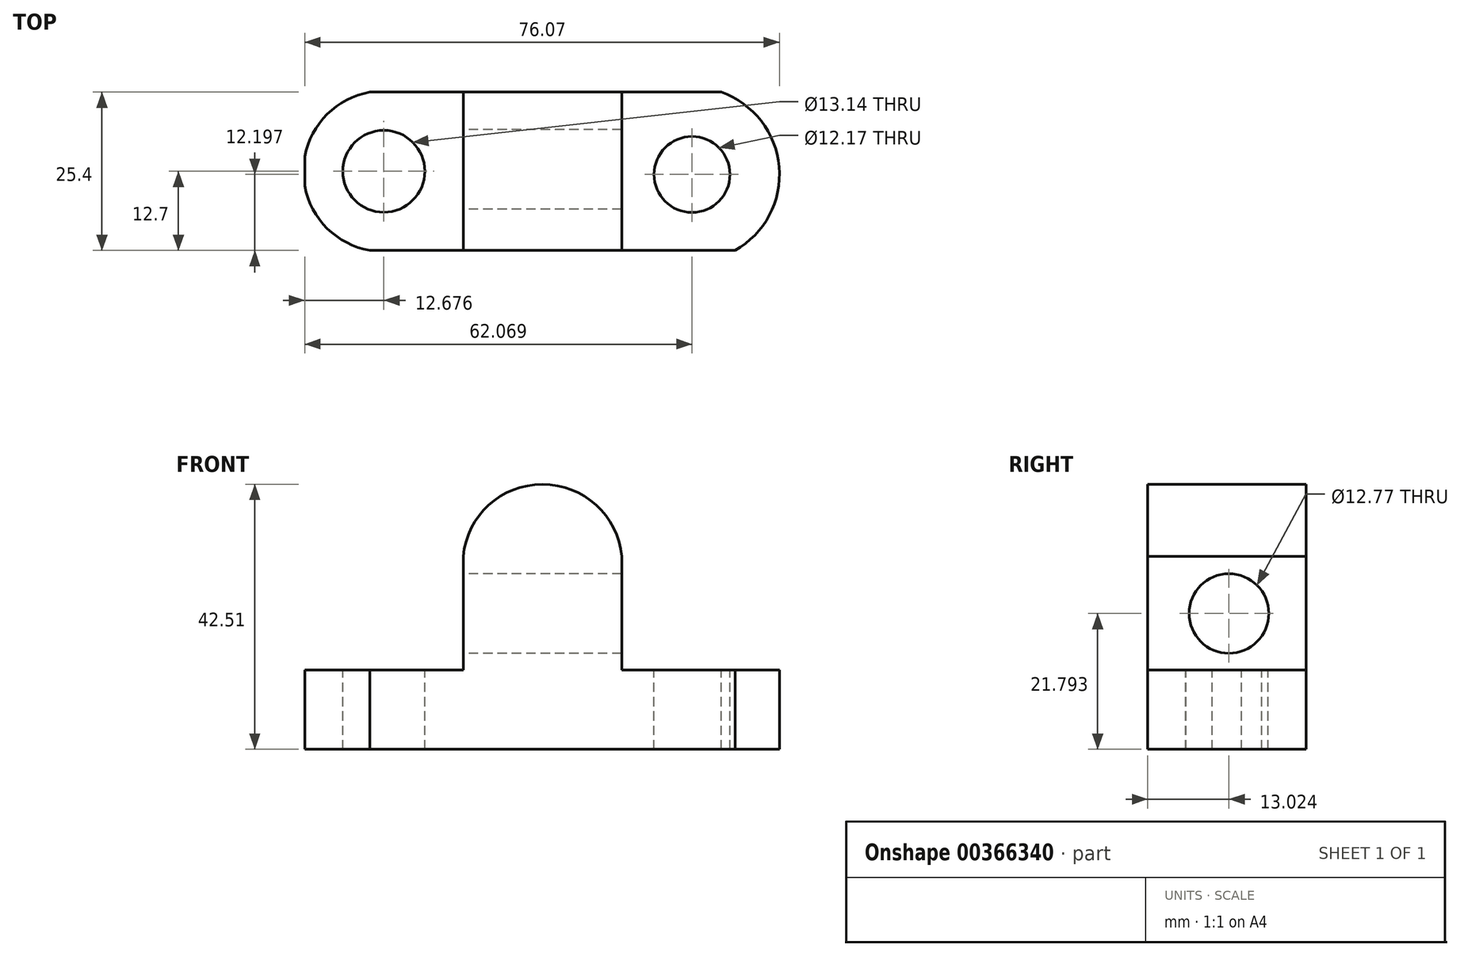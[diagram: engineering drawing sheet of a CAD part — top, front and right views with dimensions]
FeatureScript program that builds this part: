
annotation { "Feature Type Name" : "Feature", "Feature Type Description" : "" }
export const myFeature = defineFeature(function(context is Context, id is Id, definition is map)
    precondition{}
    {
        {
            var Q0;
            Q0=qCreatedBy(makeId("Front.planeOp"),FACE);
            var sketch = newSketch(context, id + "F0", { "sketchPlane" : qUnion([Q0])});
            skLineSegment(sketch, "E0", {"start": v(0, 0) * mm, "end": v(0, 12.7) * mm});
            skLineSegment(sketch, "E1", {"start": v(0, 12.7) * mm, "end": v(25.4, 12.7) * mm});
            skLineSegment(sketch, "E2", {"start": v(25.4, 12.7) * mm, "end": v(25.4, 44.45) * mm});
            skLineSegment(sketch, "E3", {"start": v(25.4, 44.45) * mm, "end": v(50.8, 44.45) * mm});
            skLineSegment(sketch, "E4", {"start": v(50.8, 44.45) * mm, "end": v(50.8, 12.7) * mm});
            skLineSegment(sketch, "E5", {"start": v(50.8, 12.7) * mm, "end": v(76.2, 12.7) * mm});
            skLineSegment(sketch, "E6", {"start": v(76.2, 12.7) * mm, "end": v(76.2, 0) * mm});
            skLineSegment(sketch, "E7", {"start": v(76.2, 0) * mm, "end": v(0, 0) * mm});
            skSolve(sketch);
        }
        {
            var Q0;
            Q0 = qSketchRegion(id + "F0", true);
            extrude(context, id + "F1", {"entities" : qUnion([Q0]), "depth" : 25.4 * mm});
        }
        {
            var Q0;
            Q0=makeQuery(id+"F1.opExtrude","CAP_FACE",FACE,{"disambiguationData":[OSD([sQuery(id+"F0.wireOp",EDGE,"E0"),sQuery(id+"F0.wireOp",EDGE,"E1"),sQuery(id+"F0.wireOp",EDGE,"E2"),sQuery(id+"F0.wireOp",EDGE,"E3"),sQuery(id+"F0.wireOp",EDGE,"E4"),sQuery(id+"F0.wireOp",EDGE,"E5"),sQuery(id+"F0.wireOp",EDGE,"E6"),sQuery(id+"F0.wireOp",EDGE,"E7")])],"isStart":false});
            var sketch = newSketch(context, id + "F2", { "sketchPlane" : qUnion([Q0])});
            skArc(sketch, "E8", {"start": v(50.8, 28.58) * mm, "mid": v(38.1, 42.5) * mm, "end": v(25.4, 28.58) * mm});
            skSolve(sketch);
        }
        {
            var Q0;
            Q0 = qSketchRegion(id + "F2", true);
            var Q1;
            {var subQ5=makeQuery(id+"F1.opExtrude","CAP_EDGE",EDGE,{"disambiguationData":[OSD([sQuery(id+"F0.wireOp",EDGE,"E3")])],"isStart":false});Q1=makeQuery(id+"F2.imprint","IMPRINT",FACE,{"disambiguationData":[TD([[makeQuery(id+"F2.imprint","IMPRINT",EDGE,{"derivedFrom":subQ5}),-1.0]])]});}
            extrude(context, id + "F3", {"entities" : qUnion([Q0, Q1]), "operationType" : NewBodyOperationType.REMOVE, "oppositeDirection" : true, "depth" : 25.4 * mm});
        }
        {
            var Q0;
            Q0=makeQuery(id+"F1.opExtrude","SWEPT_FACE",FACE,{"disambiguationData":[OSD([sQuery(id+"F0.wireOp",EDGE,"E1")])]});
            var sketch = newSketch(context, id + "F4", { "sketchPlane" : qUnion([Q0])});
            skArc(sketch, "E9", {"start": v(10.45, 0) * mm, "mid": v(-0.22, -12.7) * mm, "end": v(10.45, -25.4) * mm});
            skArc(sketch, "E10", {"start": v(65.94, -25.4) * mm, "mid": v(76.07, -12.37) * mm, "end": v(65.13, 0) * mm});
            skSolve(sketch);
        }
        {
            var Q0;
            {var subQ0=sQuery(id+"F4.wireOp",EDGE,"E9");var subQ1=sQuery(id+"F0.wireOp",EDGE,"E1");var subQ2=makeQuery(id+"F1.opExtrude","CAP_EDGE",EDGE,{"disambiguationData":[OSD([subQ1])],"isStart":true});var subQ3=makeQuery(id+"F4.imprint","INTERSECT",VERTEX,{"derivedFrom":[subQ2,subQ0]});Q0=makeQuery(id+"F4.imprint","IMPRINT",FACE,{"disambiguationData":[TD([[makeQuery(id+"F4.imprint","IMPRINT",EDGE,{"disambiguationData":[TD([[subQ3,-1.0]])],"derivedFrom":subQ0}),-1.0]])]});}
            var Q1;
            {var subQ0=sQuery(id+"F4.wireOp",EDGE,"E9");var subQ1=sQuery(id+"F0.wireOp",EDGE,"E1");var subQ2=makeQuery(id+"F1.opExtrude","CAP_EDGE",EDGE,{"disambiguationData":[OSD([subQ1])],"isStart":false});var subQ3=makeQuery(id+"F4.imprint","INTERSECT",VERTEX,{"derivedFrom":[subQ2,subQ0]});Q1=makeQuery(id+"F4.imprint","IMPRINT",FACE,{"disambiguationData":[TD([[makeQuery(id+"F4.imprint","IMPRINT",EDGE,{"disambiguationData":[TD([[subQ3,1.0]])],"derivedFrom":subQ0}),-1.0]])]});}
            extrude(context, id + "F5", {"entities" : qUnion([Q0, Q1]), "operationType" : NewBodyOperationType.REMOVE, "oppositeDirection" : true, "depth" : 25.4 * mm});
        }
        {
            var Q0;
            Q0=makeQuery(id+"F1.opExtrude","SWEPT_FACE",FACE,{"disambiguationData":[OSD([sQuery(id+"F0.wireOp",EDGE,"E5")])]});
            var sketch = newSketch(context, id + "F6", { "sketchPlane" : qUnion([Q0])});
            skArc(sketch, "E11", {"start": v(68.95, -25.4) * mm, "mid": v(76.02, -11.99) * mm, "end": v(66.74, 0) * mm});
            skSolve(sketch);
        }
        {
            var Q0;
            Q0 = qSketchRegion(id + "F6", true);
            var Q1;
            {var subQ0=sQuery(id+"F6.wireOp",EDGE,"E11");Q1=makeQuery(id+"F6.imprint","IMPRINT",FACE,{"disambiguationData":[TD([[makeQuery(id+"F6.imprint","IMPRINT",EDGE,{"derivedFrom":subQ0}),-1.0]])]});}
            extrude(context, id + "F7", {"entities" : qUnion([Q0, Q1]), "operationType" : NewBodyOperationType.REMOVE, "oppositeDirection" : true, "depth" : 25.4 * mm});
        }
        {
            var Q0;
            Q0=makeQuery(id+"F1.opExtrude","SWEPT_FACE",FACE,{"disambiguationData":[OSD([sQuery(id+"F0.wireOp",EDGE,"E1")])]});
            var sketch = newSketch(context, id + "F8", { "sketchPlane" : qUnion([Q0])});
            skCircle(sketch, "E12", {"center": v(12.68, -12.7) * mm, "radius": 6.57 * mm});
            skSolve(sketch);
        }
        {
            var Q0;
            Q0=makeQuery(id+"F8.imprint","IMPRINT",FACE,{"disambiguationData":[TD([[makeQuery(id+"F8.imprint","IMPRINT",EDGE,{"derivedFrom":sQuery(id+"F8.wireOp",EDGE,"E12")}),1.0]])]});
            extrude(context, id + "F9", {"entities" : qUnion([Q0]), "operationType" : NewBodyOperationType.REMOVE, "oppositeDirection" : true, "depth" : 25.4 * mm});
        }
        {
            var Q0;
            Q0=makeQuery(id+"F1.opExtrude","SWEPT_FACE",FACE,{"disambiguationData":[OSD([sQuery(id+"F0.wireOp",EDGE,"E5")])]});
            var sketch = newSketch(context, id + "F10", { "sketchPlane" : qUnion([Q0])});
            skCircle(sketch, "E13", {"center": v(62.07, -13.2) * mm, "radius": 6.09 * mm});
            skSolve(sketch);
        }
        {
            var Q0;
            Q0=makeQuery(id+"F10.imprint","IMPRINT",FACE,{"disambiguationData":[TD([[makeQuery(id+"F10.imprint","IMPRINT",EDGE,{"derivedFrom":sQuery(id+"F10.wireOp",EDGE,"E13")}),1.0]])]});
            extrude(context, id + "F11", {"entities" : qUnion([Q0]), "operationType" : NewBodyOperationType.REMOVE, "oppositeDirection" : true, "depth" : 25.4 * mm});
        }
        {
            var Q0;
            Q0=makeQuery(id+"F1.opExtrude","SWEPT_FACE",FACE,{"disambiguationData":[OSD([sQuery(id+"F0.wireOp",EDGE,"E2")])]});
            var sketch = newSketch(context, id + "F12", { "sketchPlane" : qUnion([Q0])});
            skCircle(sketch, "E14", {"center": v(12.38, 21.8) * mm, "radius": 6.38 * mm});
            skSolve(sketch);
        }
        {
            var Q0;
            Q0 = qSketchRegion(id + "F12", true);
            extrude(context, id + "F13", {"entities" : qUnion([Q0]), "operationType" : NewBodyOperationType.REMOVE, "oppositeDirection" : true, "depth" : 25.4 * mm});
        }
    });
